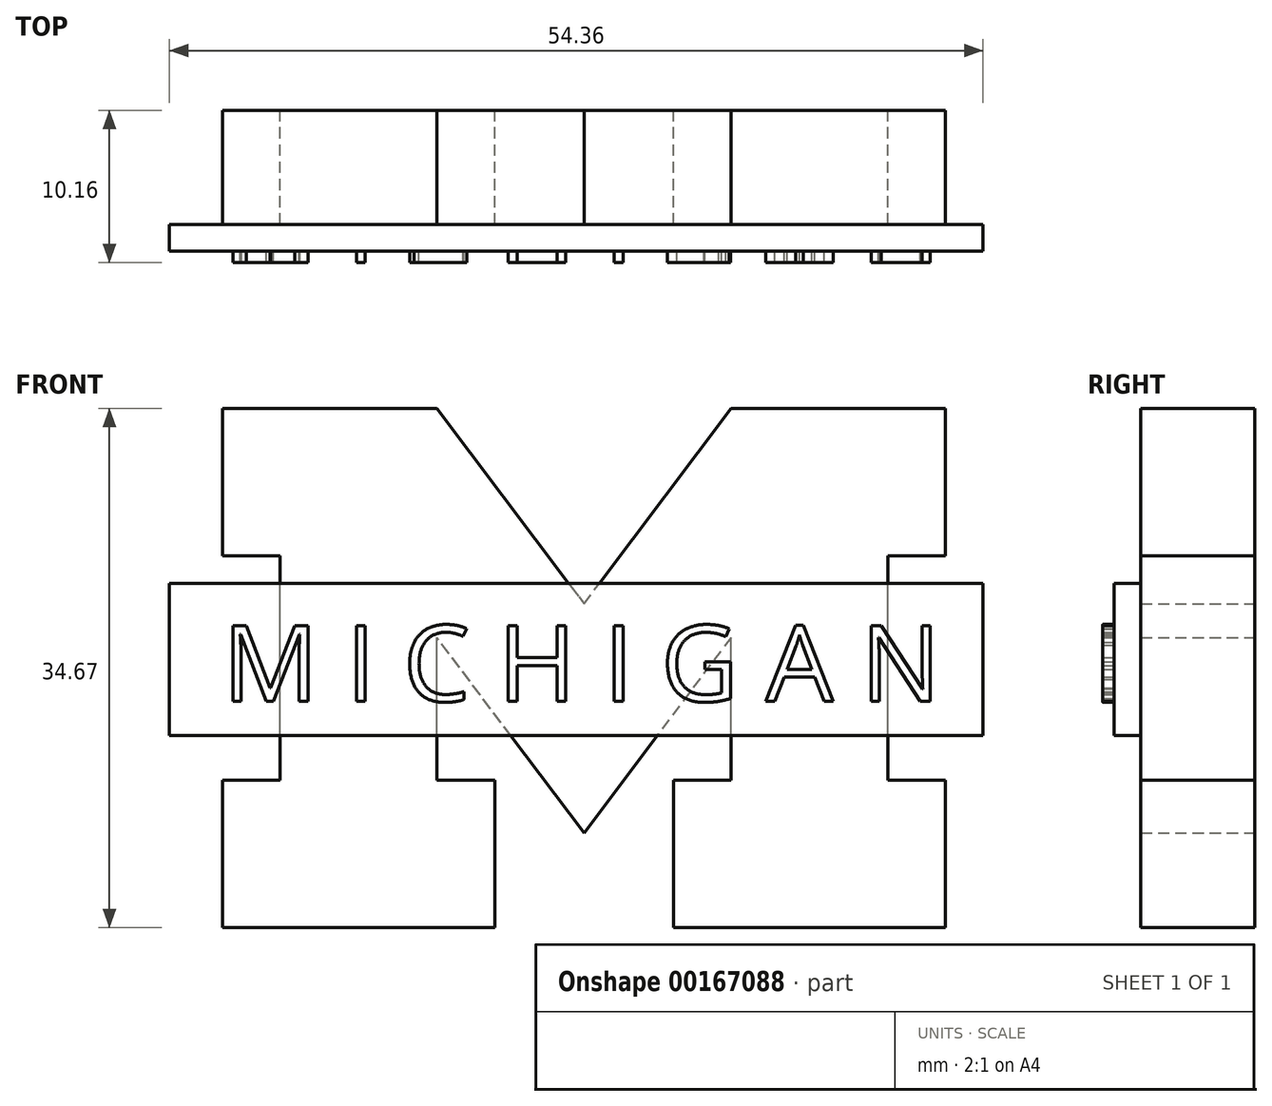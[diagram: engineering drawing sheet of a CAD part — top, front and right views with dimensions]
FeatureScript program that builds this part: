
annotation { "Feature Type Name" : "Feature", "Feature Type Description" : "" }
export const myFeature = defineFeature(function(context is Context, id is Id, definition is map)
    precondition{}
    {
        {
            var Q0;
            Q0=qCreatedBy(makeId("Front.planeOp"),FACE);
            var sketch = newSketch(context, id + "F0", { "sketchPlane" : qUnion([Q0])});
            skLineSegment(sketch, "E0", {"start": v(0, 0) * mm, "end": v(18.19, 0) * mm});
            skLineSegment(sketch, "E1", {"start": v(18.19, 0) * mm, "end": v(18.19, 9.83) * mm});
            skLineSegment(sketch, "E2", {"start": v(0, 0) * mm, "end": v(0, 9.83) * mm});
            skLineSegment(sketch, "E3", {"start": v(0, 9.83) * mm, "end": v(3.86, 9.83) * mm});
            skLineSegment(sketch, "E4", {"start": v(3.86, 9.83) * mm, "end": v(3.86, 24.84) * mm});
            skLineSegment(sketch, "E5", {"start": v(3.86, 24.84) * mm, "end": v(0, 24.84) * mm});
            skLineSegment(sketch, "E6", {"start": v(0, 24.84) * mm, "end": v(0, 34.67) * mm});
            skLineSegment(sketch, "E7", {"start": v(0, 34.67) * mm, "end": v(14.33, 34.67) * mm});
            skLineSegment(sketch, "E8", {"start": v(30.12, 0) * mm, "end": v(30.12, 9.83) * mm});
            skLineSegment(sketch, "E9", {"start": v(30.12, 9.83) * mm, "end": v(33.99, 9.83) * mm});
            skLineSegment(sketch, "E10", {"start": v(18.19, 9.83) * mm, "end": v(14.33, 9.83) * mm});
            skLineSegment(sketch, "E11", {"start": v(30.12, 0) * mm, "end": v(48.31, 0) * mm});
            skLineSegment(sketch, "E12", {"start": v(48.31, 0) * mm, "end": v(48.31, 9.83) * mm});
            skLineSegment(sketch, "E13", {"start": v(48.31, 9.83) * mm, "end": v(44.45, 9.83) * mm});
            skLineSegment(sketch, "E14", {"start": v(44.45, 9.83) * mm, "end": v(44.45, 24.84) * mm});
            skLineSegment(sketch, "E15", {"start": v(44.45, 24.84) * mm, "end": v(48.31, 24.84) * mm});
            skLineSegment(sketch, "E16", {"start": v(48.31, 24.84) * mm, "end": v(48.31, 34.67) * mm});
            skLineSegment(sketch, "E17", {"start": v(48.31, 34.67) * mm, "end": v(33.99, 34.67) * mm});
            skLineSegment(sketch, "E18", {"start": v(14.33, 9.83) * mm, "end": v(14.33, 19.38) * mm});
            skLineSegment(sketch, "E19", {"start": v(33.99, 9.83) * mm, "end": v(33.99, 19.38) * mm});
            skLineSegment(sketch, "E20", {"start": v(33.99, 19.38) * mm, "end": v(24.16, 6.34) * mm});
            skLineSegment(sketch, "E21", {"start": v(24.16, 6.34) * mm, "end": v(14.33, 19.38) * mm});
            skLineSegment(sketch, "E22", {"start": v(14.33, 34.67) * mm, "end": v(24.16, 21.63) * mm});
            skLineSegment(sketch, "E23", {"start": v(24.16, 21.63) * mm, "end": v(33.99, 34.67) * mm});
            skSolve(sketch);
        }
        {
            var Q0;
            Q0 = qSketchRegion(id + "F0", true);
            extrude(context, id + "F1", {"entities" : qUnion([Q0]), "depth" : 7.62 * mm});
        }
        {
            var Q0;
            Q0=makeQuery(id+"F1.opExtrude","CAP_FACE",FACE,{"disambiguationData":[OSD([sQuery(id+"F0.wireOp",EDGE,"E0"),sQuery(id+"F0.wireOp",EDGE,"E1"),sQuery(id+"F0.wireOp",EDGE,"E2"),sQuery(id+"F0.wireOp",EDGE,"E3"),sQuery(id+"F0.wireOp",EDGE,"E4"),sQuery(id+"F0.wireOp",EDGE,"E5"),sQuery(id+"F0.wireOp",EDGE,"E6"),sQuery(id+"F0.wireOp",EDGE,"E7"),sQuery(id+"F0.wireOp",EDGE,"E8"),sQuery(id+"F0.wireOp",EDGE,"E9"),sQuery(id+"F0.wireOp",EDGE,"E10"),sQuery(id+"F0.wireOp",EDGE,"E11"),sQuery(id+"F0.wireOp",EDGE,"E12"),sQuery(id+"F0.wireOp",EDGE,"E13"),sQuery(id+"F0.wireOp",EDGE,"E14"),sQuery(id+"F0.wireOp",EDGE,"E15"),sQuery(id+"F0.wireOp",EDGE,"E16"),sQuery(id+"F0.wireOp",EDGE,"E17"),sQuery(id+"F0.wireOp",EDGE,"E18"),sQuery(id+"F0.wireOp",EDGE,"E19"),sQuery(id+"F0.wireOp",EDGE,"E20"),sQuery(id+"F0.wireOp",EDGE,"E21"),sQuery(id+"F0.wireOp",EDGE,"E22"),sQuery(id+"F0.wireOp",EDGE,"E23")])],"isStart":false});
            var sketch = newSketch(context, id + "F2", { "sketchPlane" : qUnion([Q0])});
            skLineSegment(sketch, "E24", {"start": v(-3.54, 23) * mm, "end": v(50.82, 23) * mm});
            skLineSegment(sketch, "E25", {"start": v(-3.54, 23) * mm, "end": v(-3.54, 12.84) * mm});
            skLineSegment(sketch, "E26", {"start": v(-3.54, 12.84) * mm, "end": v(50.82, 12.84) * mm});
            skLineSegment(sketch, "E27", {"start": v(50.82, 12.84) * mm, "end": v(50.82, 23) * mm});
            skPoint(sketch, "E28.firstSnap0", {"position": v(0, 29.76) * mm});
            skSolve(sketch);
        }
        {
            var Q0;
            Q0 = qSketchRegion(id + "F2", true);
            extrude(context, id + "F3", {"entities" : qUnion([Q0]), "operationType" : NewBodyOperationType.ADD, "depth" : 1.78 * mm});
        }
        {
            var Q0;
            Q0=makeQuery(id+"F3.opExtrude","CAP_FACE",FACE,{"disambiguationData":[OSD([sQuery(id+"F2.wireOp",EDGE,"E24"),sQuery(id+"F2.wireOp",EDGE,"E25"),sQuery(id+"F2.wireOp",EDGE,"E26"),sQuery(id+"F2.wireOp",EDGE,"E27")])],"isStart":false});
            var sketch = newSketch(context, id + "F4", { "sketchPlane" : qUnion([Q0])});
            skText(sketch, "E29", { "text": "M I C H I G A N", "fontName": "OpenSans-Regular.ttf"});
            const initialGuessF4  = {"E29": [0, 0.01511, 1, 0, 0.00511]};
            skSetInitialGuess(sketch, initialGuessF4);
            skSolve(sketch);
        }
        {
            var Q0;
            Q0 = qSketchRegion(id + "F4", true);
            extrude(context, id + "F5", {"entities" : qUnion([Q0]), "operationType" : NewBodyOperationType.ADD, "depth" : 0.76 * mm});
        }
    });
